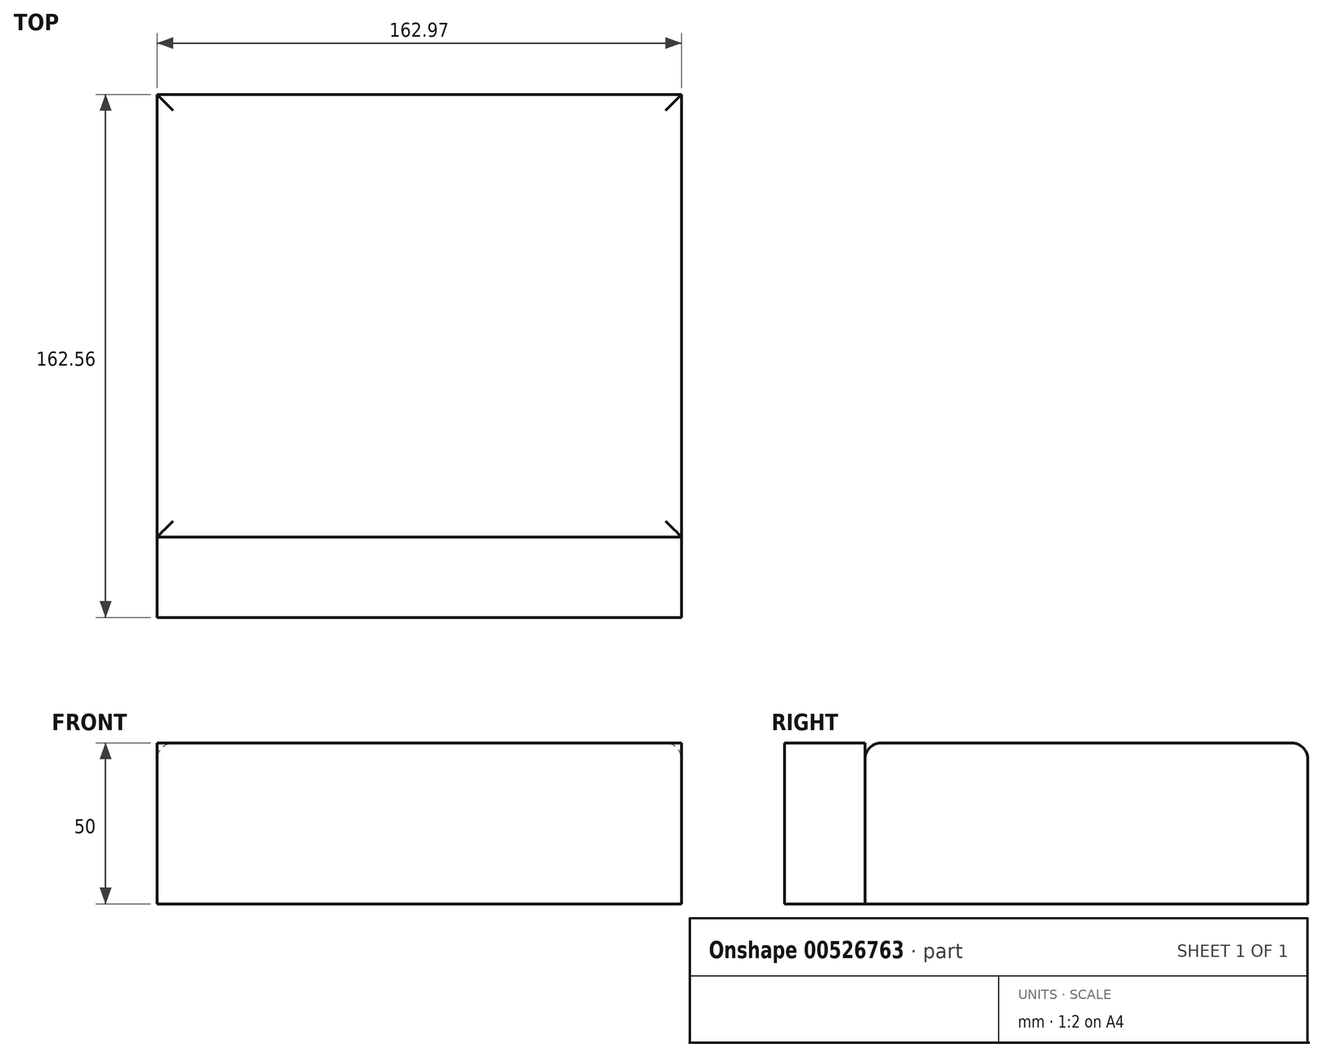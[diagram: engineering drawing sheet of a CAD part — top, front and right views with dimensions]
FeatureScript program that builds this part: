
annotation { "Feature Type Name" : "Feature", "Feature Type Description" : "" }
export const myFeature = defineFeature(function(context is Context, id is Id, definition is map)
    precondition{}
    {
        {
            var Q0;
            Q0=qCreatedBy(makeId("Top.planeOp"),FACE);
            var sketch = newSketch(context, id + "F0", { "sketchPlane" : qUnion([Q0])});
            skLineSegment(sketch, "E0.bottom", {"start": v(89.08, 74.47) * mm, "end": v(-73.9, 74.47) * mm});
            skLineSegment(sketch, "E0.top", {"start": v(89.08, -63.1) * mm, "end": v(-73.9, -63.1) * mm});
            skLineSegment(sketch, "E0.left", {"start": v(89.08, 74.47) * mm, "end": v(89.08, -63.1) * mm});
            skLineSegment(sketch, "E0.right", {"start": v(-73.9, 74.47) * mm, "end": v(-73.9, -63.1) * mm});
            skSolve(sketch);
        }
        {
            var Q0;
            Q0=makeQuery(id+"F0.imprint","IMPRINT",FACE,{"disambiguationData":[TD([[makeQuery(id+"F0.imprint","IMPRINT",EDGE,{"derivedFrom":sQuery(id+"F0.wireOp",EDGE,"E0.bottom")}),1.0]])]});
            extrude(context, id + "F1", {"entities" : qUnion([Q0]), "depth" : 50 * mm, "offsetDistance" : 25 * mm});
        }
        {
            var Q0;
            Q0=makeQuery(id+"F1.opExtrude","SWEPT_FACE",FACE,{"disambiguationData":[OSD([sQuery(id+"F0.wireOp",EDGE,"E0.top")])]});
            extrude(context, id + "F2", {"entities" : qUnion([Q0]), "depth" : 25 * mm, "offsetDistance" : 25 * mm});
        }
        {
            var Q0;
            Q0=makeQuery(id+"F1.opExtrude","CAP_EDGE",EDGE,{"disambiguationData":[OSD([sQuery(id+"F0.wireOp",EDGE,"E0.left")])],"isStart":false});
            var Q1;
            Q1=makeQuery(id+"F1.opExtrude","CAP_EDGE",EDGE,{"disambiguationData":[OSD([sQuery(id+"F0.wireOp",EDGE,"E0.top")])],"isStart":false});
            var Q2;
            Q2=makeQuery(id+"F1.opExtrude","CAP_EDGE",EDGE,{"disambiguationData":[OSD([sQuery(id+"F0.wireOp",EDGE,"E0.right")])],"isStart":false});
            var Q3;
            Q3=makeQuery(id+"F1.opExtrude","CAP_EDGE",EDGE,{"disambiguationData":[OSD([sQuery(id+"F0.wireOp",EDGE,"E0.bottom")])],"isStart":false});
            fillet(context, id + "F3", {"entities" : qUnion([Q0, Q1, Q2, Q3]), "radius" : 5 * mm, "tangentPropagation" : true, "allowEdgeOverflow" : false});
        }
    });
